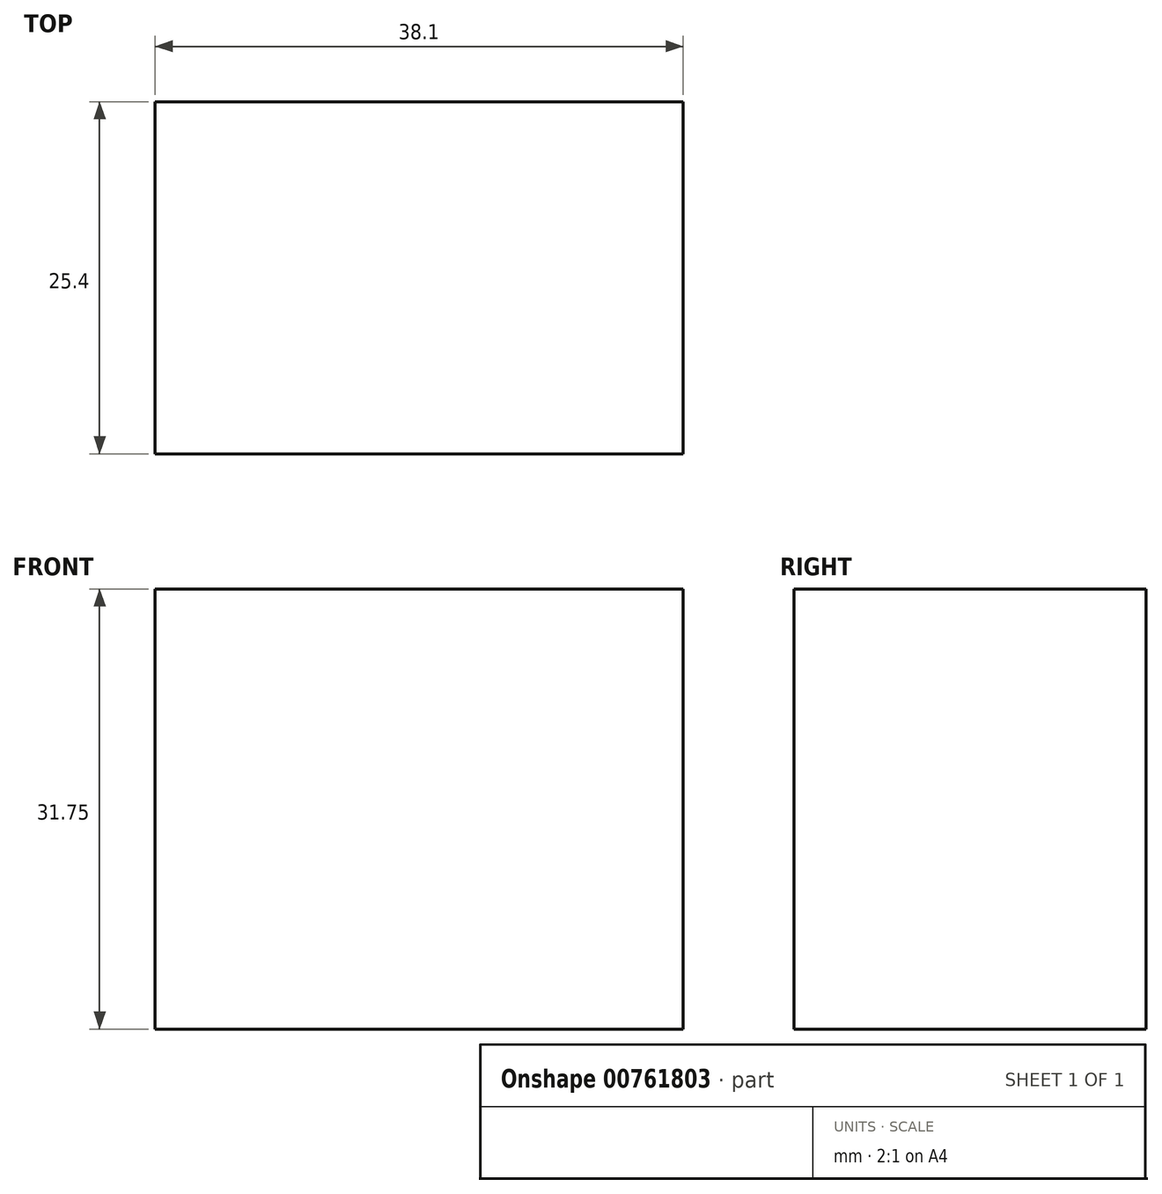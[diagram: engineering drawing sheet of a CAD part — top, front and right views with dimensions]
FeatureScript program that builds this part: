
annotation { "Feature Type Name" : "Feature", "Feature Type Description" : "" }
export const myFeature = defineFeature(function(context is Context, id is Id, definition is map)
    precondition{}
    {
        {
            var Q0;
            Q0=qCreatedBy(makeId("Front.planeOp"),FACE);
            var sketch = newSketch(context, id + "F0", { "sketchPlane" : qUnion([Q0])});
            skLineSegment(sketch, "E0", {"start": v(0, 0) * mm, "end": v(0, 31.75) * mm});
            skLineSegment(sketch, "E1", {"start": v(0, 31.75) * mm, "end": v(38.1, 31.75) * mm});
            skLineSegment(sketch, "E2", {"start": v(38.1, 31.75) * mm, "end": v(38.1, 0) * mm});
            skLineSegment(sketch, "E3", {"start": v(38.1, 0) * mm, "end": v(0, 0) * mm});
            skSolve(sketch);
        }
        {
            var Q0;
            Q0=makeQuery(id+"F0.imprint","IMPRINT",FACE,{"disambiguationData":[TD([[makeQuery(id+"F0.imprint","IMPRINT",EDGE,{"derivedFrom":sQuery(id+"F0.wireOp",EDGE,"E0")}),-1.0]])]});
            extrude(context, id + "F1", {"entities" : qUnion([Q0]), "depth" : 25.4 * mm, "offsetDistance" : 25.4 * mm});
        }
    });
